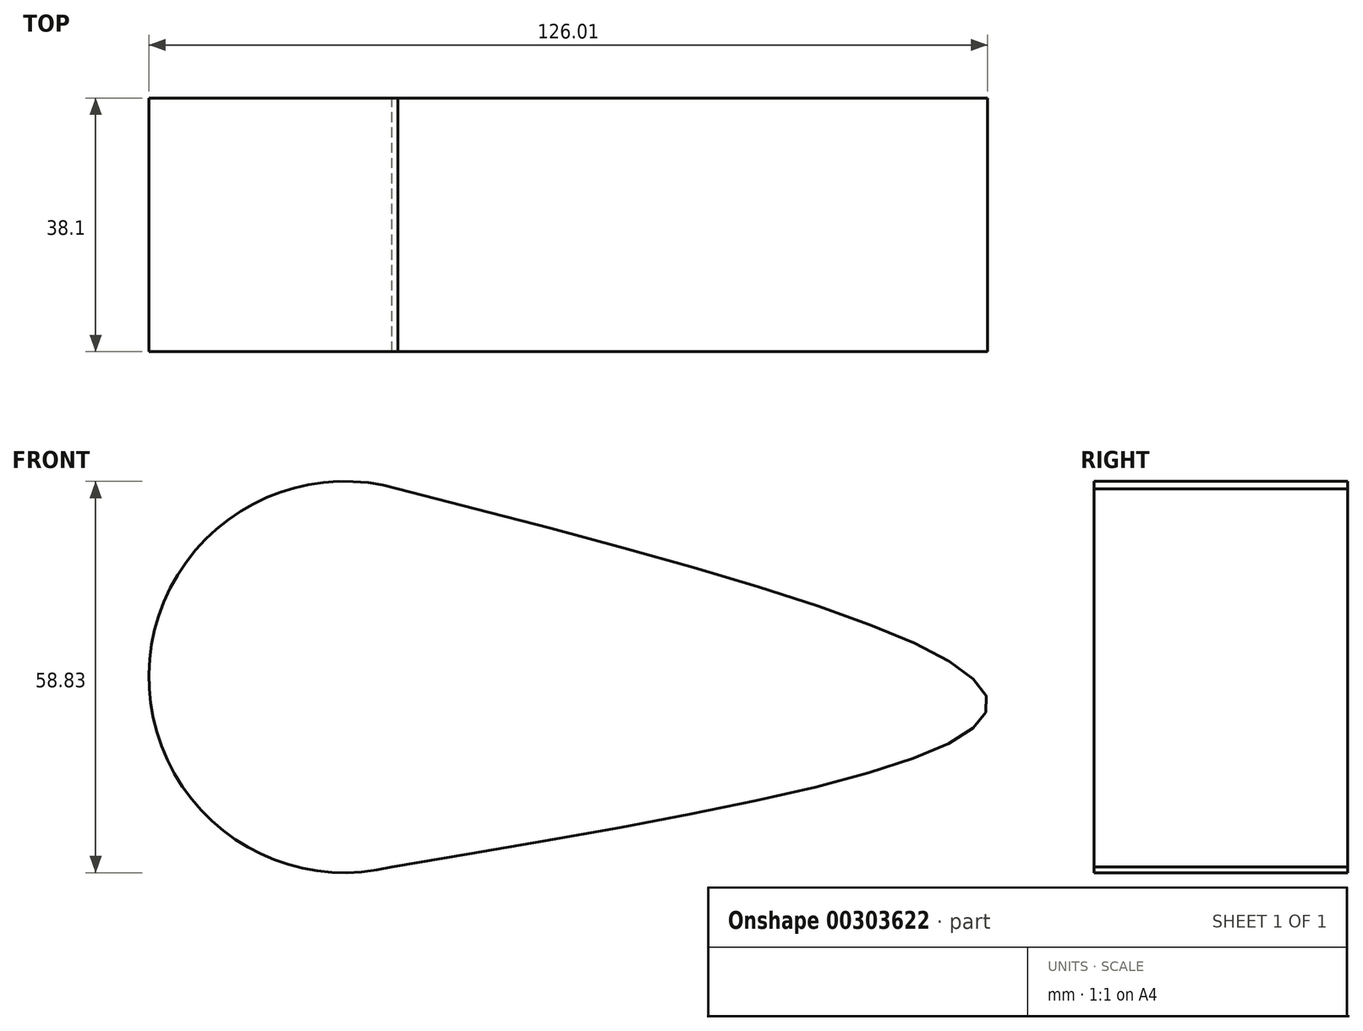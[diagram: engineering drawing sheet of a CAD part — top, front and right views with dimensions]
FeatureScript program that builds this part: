
annotation { "Feature Type Name" : "Feature", "Feature Type Description" : "" }
export const myFeature = defineFeature(function(context is Context, id is Id, definition is map)
    precondition{}
    {
        {
            var Q0;
            Q0=qCreatedBy(makeId("Front.planeOp"),FACE);
            var sketch = newSketch(context, id + "F0", { "sketchPlane" : qUnion([Q0])});
            skArc(sketch, "E0", {"start": v(-63.8, 56.86) * mm, "mid": v(-101.21, 29.03) * mm, "end": v(-64.73, 0) * mm});
            skFitSpline(sketch, "E1", {"points": [v(-63.8, 56.86) * mm, v(24.8, 24.36) * mm, v(-64.73, 0) * mm], "startDerivative": vector(265.9, -68.69) * mm, "endDerivative": vector(-268.5, -45) * mm});
            skSolve(sketch);
        }
        {
            var Q0;
            Q0 = qSketchRegion(id + "F0", true);
            extrude(context, id + "F1", {"entities" : qUnion([Q0]), "endBound" : BoundingType.SYMMETRIC, "depth" : 38.1 * mm});
        }
    });
